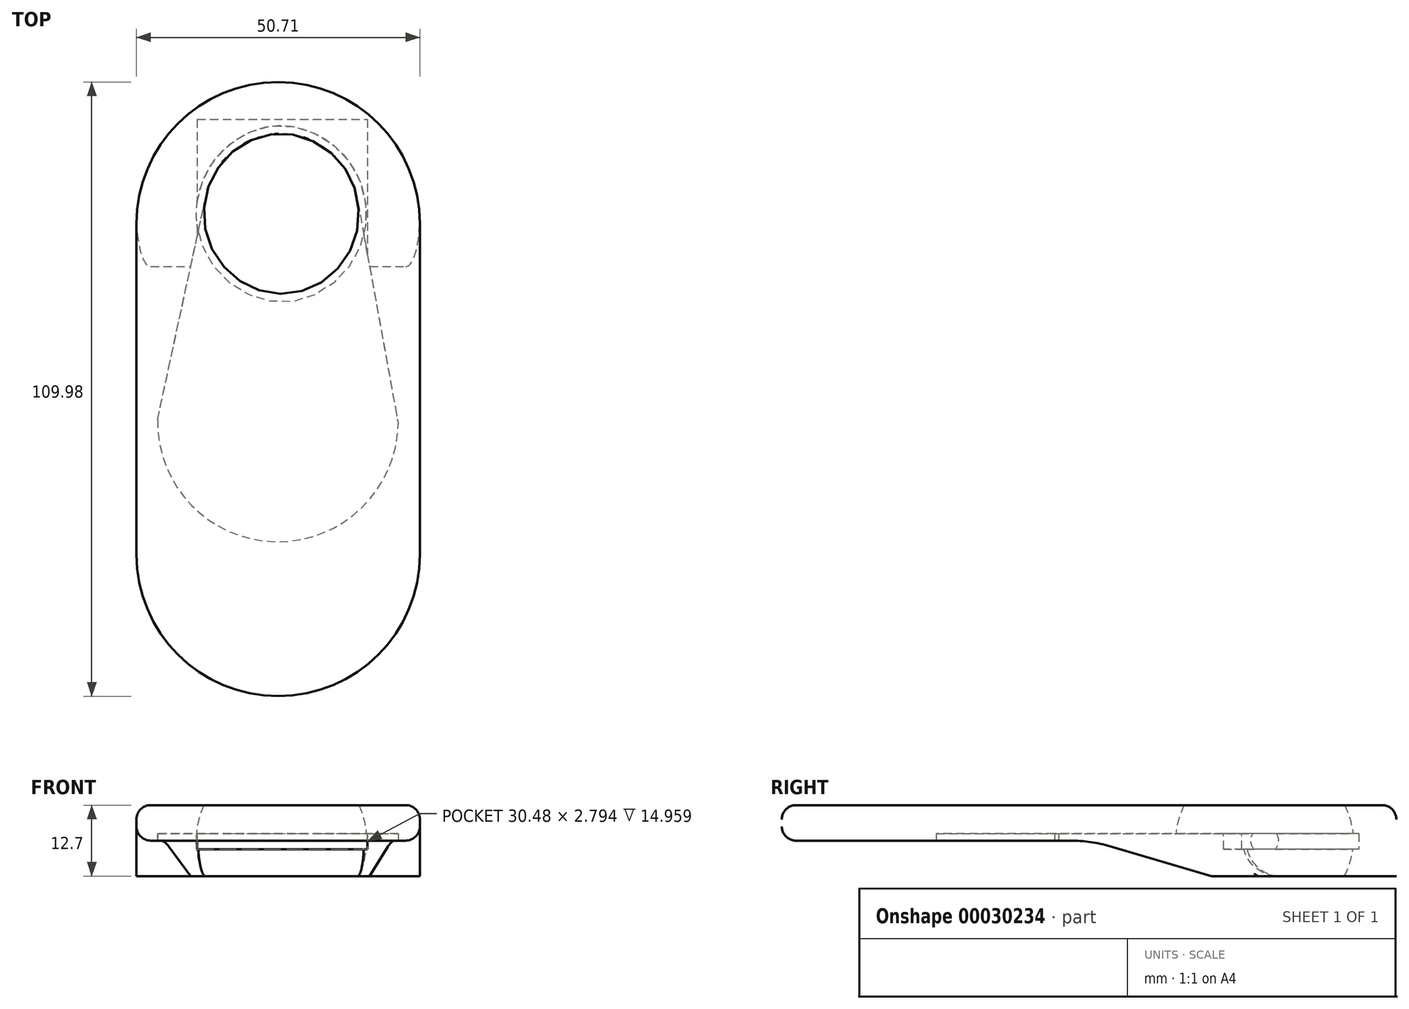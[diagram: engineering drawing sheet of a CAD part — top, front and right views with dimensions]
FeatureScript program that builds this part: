
annotation { "Feature Type Name" : "Feature", "Feature Type Description" : "" }
export const myFeature = defineFeature(function(context is Context, id is Id, definition is map)
    precondition{}
    {
        {
            var Q0;
            Q0=qCreatedBy(makeId("Top.planeOp"),FACE);
            var sketch = newSketch(context, id + "F0", { "sketchPlane" : qUnion([Q0])});
            skLineSegment(sketch, "E0.bottom", {"start": v(-12.22, 60.39) * mm, "end": v(18.26, 60.39) * mm});
            skLineSegment(sketch, "E0.top", {"start": v(-12.22, 28.64) * mm, "end": v(18.26, 28.64) * mm});
            skLineSegment(sketch, "E0.left", {"start": v(-12.22, 60.39) * mm, "end": v(-12.22, 28.64) * mm});
            skLineSegment(sketch, "E0.right", {"start": v(18.26, 60.39) * mm, "end": v(18.26, 28.64) * mm});
            skSolve(sketch);
        }
        {
            var Q0;
            Q0=qCreatedBy(makeId("Top.planeOp"),FACE);
            var sketch = newSketch(context, id + "F1", { "sketchPlane" : qUnion([Q0])});
            skArc(sketch, "E1", {"start": v(3.76, 27.52) * mm, "mid": v(18.06, 44.36) * mm, "end": v(1.92, 59.44) * mm});
            skLineSegment(sketch, "E2", {"start": v(3.76, 27.52) * mm, "end": v(1.92, 59.44) * mm});
            skSolve(sketch);
        }
        {
            var Q0;
            Q0=makeQuery(id+"F1.imprint","IMPRINT",FACE,{"disambiguationData":[TD([[makeQuery(id+"F1.imprint","IMPRINT",EDGE,{"derivedFrom":sQuery(id+"F1.wireOp",EDGE,"E1")}),1.0]])]});
            var Q1;
            Q1=sQuery(id+"F1.wireOp",EDGE,"E1");
            var Q2;
            Q2=sQuery(id+"F1.wireOp",EDGE,"E2");
            revolve(context, id + "F2", {"entities" : qUnion([Q0]), "surfaceEntities" : qUnion([Q1]), "axis" : qUnion([Q2]), "revolveType" : RevolveType.FULL});
        }
        {
            var Q0;
            Q0=makeQuery(id+"F0.imprint","IMPRINT",FACE,{"disambiguationData":[TD([[makeQuery(id+"F0.imprint","IMPRINT",EDGE,{"derivedFrom":sQuery(id+"F0.wireOp",EDGE,"E0.bottom")}),-1.0]])]});
            extrude(context, id + "F3", {"entities" : qUnion([Q0]), "depth" : 1.27 * mm, "hasSecondDirection" : true, "secondDirectionOppositeDirection" : true, "secondDirectionDepth" : 1.52 * mm});
        }
        {
            var Q0;
            Q0=qCreatedBy(makeId("Top.planeOp"),FACE);
            var sketch = newSketch(context, id + "F4", { "sketchPlane" : qUnion([Q0])});
            skLineSegment(sketch, "E3.bottom", {"start": v(-23.08, 67.1) * mm, "end": v(27.63, 67.1) * mm});
            skLineSegment(sketch, "E3.top", {"start": v(-23.08, -42.89) * mm, "end": v(27.63, -42.89) * mm});
            skLineSegment(sketch, "E3.left", {"start": v(-23.08, 67.1) * mm, "end": v(-23.08, -42.89) * mm});
            skLineSegment(sketch, "E3.right", {"start": v(27.63, 67.1) * mm, "end": v(27.63, -42.89) * mm});
            skSolve(sketch);
        }
        {
            var Q0;
            Q0=makeQuery(id+"F4.imprint","IMPRINT",FACE,{"disambiguationData":[TD([[makeQuery(id+"F4.imprint","IMPRINT",EDGE,{"derivedFrom":sQuery(id+"F4.wireOp",EDGE,"E3.bottom")}),-1.0]])]});
            extrude(context, id + "F5", {"entities" : qUnion([Q0]), "depth" : 6.35 * mm, "hasSecondDirection" : true, "secondDirectionOppositeDirection" : true, "secondDirectionDepth" : 6.35 * mm});
        }
        {
            var Q0;
            Q0=makeQuery(id+"F2.opRevolve","SWEPT_BODY",BODY,{"disambiguationData":[OSD([sQuery(id+"F1.wireOp",EDGE,"E1"),sQuery(id+"F1.wireOp",EDGE,"E2")])]});
            var Q1;
            Q1=makeQuery(id+"F3.opExtrude","SWEPT_BODY",BODY,{"disambiguationData":[OSD([sQuery(id+"F0.wireOp",EDGE,"E0.bottom"),sQuery(id+"F0.wireOp",EDGE,"E0.top"),sQuery(id+"F0.wireOp",EDGE,"E0.left"),sQuery(id+"F0.wireOp",EDGE,"E0.right")])]});
            booleanBodies(context, id + "F6", {"operationType" : BooleanOperationType.UNION, "tools" : qUnion([Q0, Q1])});
        }
        {
            var Q0;
            Q0=makeQuery(id+"F2.opRevolve","SWEPT_BODY",BODY,{"disambiguationData":[OSD([sQuery(id+"F1.wireOp",EDGE,"E1"),sQuery(id+"F1.wireOp",EDGE,"E2")])]});
            var Q1;
            Q1=makeQuery(id+"F5.opExtrude","SWEPT_BODY",BODY,{"disambiguationData":[OSD([sQuery(id+"F4.wireOp",EDGE,"E3.bottom"),sQuery(id+"F4.wireOp",EDGE,"E3.top"),sQuery(id+"F4.wireOp",EDGE,"E3.left"),sQuery(id+"F4.wireOp",EDGE,"E3.right")])]});
            booleanBodies(context, id + "F7", {"operationType" : BooleanOperationType.SUBTRACTION, "tools" : qUnion([Q0]), "targets" : qUnion([Q1])});
        }
        {
            var Q0;
            Q0=makeQuery(id+"F5.opExtrude","CAP_FACE",FACE,{"disambiguationData":[OSD([sQuery(id+"F4.wireOp",EDGE,"E3.bottom"),sQuery(id+"F4.wireOp",EDGE,"E3.top"),sQuery(id+"F4.wireOp",EDGE,"E3.left"),sQuery(id+"F4.wireOp",EDGE,"E3.right")])],"isStart":true});
            var sketch = newSketch(context, id + "F8", { "sketchPlane" : qUnion([Q0])});
            skArc(sketch, "E4", {"start": v(23.75, -5.94) * mm, "mid": v(1.86, 15.23) * mm, "end": v(-19.31, -6.66) * mm});
            skLineSegment(sketch, "E5", {"start": v(-19.31, -6.66) * mm, "end": v(-10.88, -45.61) * mm});
            skLineSegment(sketch, "E6", {"start": v(-10.88, -45.61) * mm, "end": v(16.54, -45.61) * mm});
            skLineSegment(sketch, "E7", {"start": v(16.54, -45.61) * mm, "end": v(23.75, -5.94) * mm});
            skSolve(sketch);
        }
        {
            var Q0;
            {var subQ4=sQuery(id+"F8.wireOp",EDGE,"E4");Q0=makeQuery(id+"F8.imprint","IMPRINT",FACE,{"disambiguationData":[TD([[makeQuery(id+"F8.imprint","IMPRINT",EDGE,{"derivedFrom":subQ4}),1.0]])]});}
            extrude(context, id + "F9", {"entities" : qUnion([Q0]), "operationType" : NewBodyOperationType.REMOVE, "oppositeDirection" : true, "depth" : 7.62 * mm});
        }
        {
            var Q0;
            Q0=makeQuery(id+"F5.opExtrude","SWEPT_FACE",FACE,{"disambiguationData":[OSD([sQuery(id+"F4.wireOp",EDGE,"E3.right")])]});
            var sketch = newSketch(context, id + "F10", { "sketchPlane" : qUnion([Q0])});
            skLineSegment(sketch, "E8", {"start": v(34.01, -6.35) * mm, "end": v(12.4, 0) * mm});
            skLineSegment(sketch, "E9", {"start": v(12.4, 0) * mm, "end": v(-42.89, 0) * mm});
            skLineSegment(sketch, "E10", {"start": v(-42.89, 0) * mm, "end": v(-42.89, -6.35) * mm});
            skLineSegment(sketch, "E11", {"start": v(-42.89, -6.35) * mm, "end": v(34.01, -6.35) * mm});
            skSolve(sketch);
        }
        {
            var Q0;
            Q0=makeQuery(id+"F10.imprint","IMPRINT",FACE,{"disambiguationData":[TD([[makeQuery(id+"F10.imprint","IMPRINT",EDGE,{"derivedFrom":sQuery(id+"F10.wireOp",EDGE,"E8")}),1.0]])]});
            extrude(context, id + "F11", {"entities" : qUnion([Q0]), "operationType" : NewBodyOperationType.REMOVE, "endBound" : BoundingType.THROUGH_ALL, "oppositeDirection" : true, "depth" : 25.4 * mm});
        }
        {
            var Q0;
            Q0=makeQuery(id+"F5.opExtrude","SWEPT_EDGE",EDGE,{"disambiguationData":[OSD([sQuery(id+"F4.wireOp",EDGE,"E3.top"),sQuery(id+"F4.wireOp",EDGE,"E3.right")])]});
            var Q1;
            Q1=makeQuery(id+"F5.opExtrude","SWEPT_EDGE",EDGE,{"disambiguationData":[OSD([sQuery(id+"F4.wireOp",EDGE,"E3.top"),sQuery(id+"F4.wireOp",EDGE,"E3.left")])]});
            var Q2;
            Q2=makeQuery(id+"F5.opExtrude","SWEPT_EDGE",EDGE,{"disambiguationData":[OSD([sQuery(id+"F4.wireOp",EDGE,"E3.bottom"),sQuery(id+"F4.wireOp",EDGE,"E3.right")])]});
            var Q3;
            Q3=makeQuery(id+"F5.opExtrude","SWEPT_EDGE",EDGE,{"disambiguationData":[OSD([sQuery(id+"F4.wireOp",EDGE,"E3.bottom"),sQuery(id+"F4.wireOp",EDGE,"E3.left")])]});
            fillet(context, id + "F12", {"entities" : qUnion([Q0, Q1, Q2, Q3]), "radius" : 25.4 * mm, "tangentPropagation" : true, "allowEdgeOverflow" : false});
        }
        {
            var Q0;
            Q0=makeQuery(id+"F11.boolean.opBoolean","COPY",EDGE,{"disambiguationData":[OD(1.0)],"derivedFrom":makeQuery(id+"F11.opExtrude","SWEPT_EDGE",EDGE,{"disambiguationData":[OSD([sQuery(id+"F4.wireOp",EDGE,"E3.right"),sQuery(id+"F10.wireOp",EDGE,"E8"),sQuery(id+"F10.wireOp",EDGE,"E11")])]})});
            var Q1;
            Q1=makeQuery(id+"F11.boolean.opBoolean","COPY",EDGE,{"disambiguationData":[OD(0.0)],"derivedFrom":makeQuery(id+"F11.opExtrude","SWEPT_EDGE",EDGE,{"disambiguationData":[OSD([sQuery(id+"F4.wireOp",EDGE,"E3.right"),sQuery(id+"F10.wireOp",EDGE,"E8"),sQuery(id+"F10.wireOp",EDGE,"E11")])]})});
            var Q2;
            Q2=makeQuery(id+"F11.boolean.opBoolean","COPY",EDGE,{"disambiguationData":[OD(0.0)],"derivedFrom":makeQuery(id+"F11.opExtrude","SWEPT_EDGE",EDGE,{"disambiguationData":[OSD([sQuery(id+"F10.wireOp",EDGE,"E8"),sQuery(id+"F10.wireOp",EDGE,"E9")])]})});
            var Q3;
            Q3=makeQuery(id+"F11.boolean.opBoolean","COPY",EDGE,{"disambiguationData":[OD(1.0)],"derivedFrom":makeQuery(id+"F11.opExtrude","SWEPT_EDGE",EDGE,{"disambiguationData":[OSD([sQuery(id+"F10.wireOp",EDGE,"E8"),sQuery(id+"F10.wireOp",EDGE,"E9")])]})});
            fillet(context, id + "F13", {"entities" : qUnion([Q0, Q1, Q2, Q3]), "radius" : 25.4 * mm, "tangentPropagation" : true, "allowEdgeOverflow" : false});
        }
        {
            var Q0;
            Q0=makeQuery(id+"F11.boolean.opBoolean","COPY",EDGE,{"derivedFrom":makeQuery(id+"F11.opExtrude","CAP_EDGE",EDGE,{"disambiguationData":[OSD([sQuery(id+"F10.wireOp",EDGE,"E9")])],"isStart":true})});
            var Q1;
            Q1=makeQuery(id+"F12.opFillet","BLEND_EDGE",EDGE,{"blendedFrom":[makeQuery(id+"F5.opExtrude","SWEPT_EDGE",EDGE,{"disambiguationData":[OSD([sQuery(id+"F4.wireOp",EDGE,"E3.top"),sQuery(id+"F4.wireOp",EDGE,"E3.right")])]}),makeQuery(id+"F11.boolean.opBoolean","COPY",FACE,{"derivedFrom":makeQuery(id+"F11.opExtrude","SWEPT_FACE",FACE,{"disambiguationData":[OSD([sQuery(id+"F10.wireOp",EDGE,"E9")])]})})],"blendedInto":[makeQuery(id+"F11.boolean.opBoolean","COPY",FACE,{"derivedFrom":makeQuery(id+"F11.opExtrude","SWEPT_FACE",FACE,{"disambiguationData":[OSD([sQuery(id+"F10.wireOp",EDGE,"E9")])]})})]});
            var Q2;
            Q2=makeQuery(id+"F12.opFillet","BLEND_EDGE",EDGE,{"blendedFrom":[makeQuery(id+"F5.opExtrude","SWEPT_EDGE",EDGE,{"disambiguationData":[OSD([sQuery(id+"F4.wireOp",EDGE,"E3.top"),sQuery(id+"F4.wireOp",EDGE,"E3.left")])]}),makeQuery(id+"F11.boolean.opBoolean","COPY",FACE,{"derivedFrom":makeQuery(id+"F11.opExtrude","SWEPT_FACE",FACE,{"disambiguationData":[OSD([sQuery(id+"F10.wireOp",EDGE,"E9")])]})})],"blendedInto":[makeQuery(id+"F11.boolean.opBoolean","COPY",FACE,{"derivedFrom":makeQuery(id+"F11.opExtrude","SWEPT_FACE",FACE,{"disambiguationData":[OSD([sQuery(id+"F10.wireOp",EDGE,"E9")])]})})]});
            var Q3;
            Q3=makeQuery(id+"F5.opExtrude","CAP_EDGE",EDGE,{"disambiguationData":[OSD([sQuery(id+"F4.wireOp",EDGE,"E3.right")])],"isStart":false});
            var Q4;
            Q4=makeQuery(id+"F5.opExtrude","CAP_EDGE",EDGE,{"disambiguationData":[OSD([sQuery(id+"F4.wireOp",EDGE,"E3.left")])],"isStart":false});
            var Q5;
            {var subQ0=sQuery(id+"F4.wireOp",EDGE,"E3.top");var subQ1=sQuery(id+"F4.wireOp",EDGE,"E3.left");Q5=makeQuery(id+"F12.opFillet","BLEND_EDGE",EDGE,{"blendedFrom":[makeQuery(id+"F5.opExtrude","SWEPT_EDGE",EDGE,{"disambiguationData":[OSD([subQ0,subQ1])]}),makeQuery(id+"F5.opExtrude","CAP_FACE",FACE,{"disambiguationData":[OSD([sQuery(id+"F4.wireOp",EDGE,"E3.bottom"),subQ0,subQ1,sQuery(id+"F4.wireOp",EDGE,"E3.right")])],"isStart":false})],"blendedInto":[makeQuery(id+"F5.opExtrude","CAP_FACE",FACE,{"disambiguationData":[OSD([sQuery(id+"F4.wireOp",EDGE,"E3.bottom"),subQ0,subQ1,sQuery(id+"F4.wireOp",EDGE,"E3.right")])],"isStart":false})]});}
            var Q6;
            {var subQ0=sQuery(id+"F4.wireOp",EDGE,"E3.top");var subQ1=sQuery(id+"F4.wireOp",EDGE,"E3.right");Q6=makeQuery(id+"F12.opFillet","BLEND_EDGE",EDGE,{"blendedFrom":[makeQuery(id+"F5.opExtrude","SWEPT_EDGE",EDGE,{"disambiguationData":[OSD([subQ0,subQ1])]}),makeQuery(id+"F5.opExtrude","CAP_FACE",FACE,{"disambiguationData":[OSD([sQuery(id+"F4.wireOp",EDGE,"E3.bottom"),subQ0,sQuery(id+"F4.wireOp",EDGE,"E3.left"),subQ1])],"isStart":false})],"blendedInto":[makeQuery(id+"F5.opExtrude","CAP_FACE",FACE,{"disambiguationData":[OSD([sQuery(id+"F4.wireOp",EDGE,"E3.bottom"),subQ0,sQuery(id+"F4.wireOp",EDGE,"E3.left"),subQ1])],"isStart":false})]});}
            var Q7;
            {var subQ0=sQuery(id+"F4.wireOp",EDGE,"E3.bottom");var subQ1=sQuery(id+"F4.wireOp",EDGE,"E3.right");Q7=makeQuery(id+"F12.opFillet","BLEND_EDGE",EDGE,{"blendedFrom":[makeQuery(id+"F5.opExtrude","SWEPT_EDGE",EDGE,{"disambiguationData":[OSD([subQ0,subQ1])]}),makeQuery(id+"F5.opExtrude","CAP_FACE",FACE,{"disambiguationData":[OSD([subQ0,sQuery(id+"F4.wireOp",EDGE,"E3.top"),sQuery(id+"F4.wireOp",EDGE,"E3.left"),subQ1])],"isStart":false})],"blendedInto":[makeQuery(id+"F5.opExtrude","CAP_FACE",FACE,{"disambiguationData":[OSD([subQ0,sQuery(id+"F4.wireOp",EDGE,"E3.top"),sQuery(id+"F4.wireOp",EDGE,"E3.left"),subQ1])],"isStart":false})]});}
            var Q8;
            {var subQ0=sQuery(id+"F4.wireOp",EDGE,"E3.bottom");var subQ1=sQuery(id+"F4.wireOp",EDGE,"E3.left");Q8=makeQuery(id+"F12.opFillet","BLEND_EDGE",EDGE,{"blendedFrom":[makeQuery(id+"F5.opExtrude","SWEPT_EDGE",EDGE,{"disambiguationData":[OSD([subQ0,subQ1])]}),makeQuery(id+"F5.opExtrude","CAP_FACE",FACE,{"disambiguationData":[OSD([subQ0,sQuery(id+"F4.wireOp",EDGE,"E3.top"),subQ1,sQuery(id+"F4.wireOp",EDGE,"E3.right")])],"isStart":false})],"blendedInto":[makeQuery(id+"F5.opExtrude","CAP_FACE",FACE,{"disambiguationData":[OSD([subQ0,sQuery(id+"F4.wireOp",EDGE,"E3.top"),subQ1,sQuery(id+"F4.wireOp",EDGE,"E3.right")])],"isStart":false})]});}
            fillet(context, id + "F14", {"entities" : qUnion([Q0, Q1, Q2, Q3, Q4, Q5, Q6, Q7, Q8]), "radius" : 2.54 * mm, "tangentPropagation" : true, "allowEdgeOverflow" : false});
        }
        {
            var Q0;
            Q0=makeQuery(id+"F5.opExtrude","CAP_FACE",FACE,{"disambiguationData":[OSD([sQuery(id+"F4.wireOp",EDGE,"E3.bottom"),sQuery(id+"F4.wireOp",EDGE,"E3.top"),sQuery(id+"F4.wireOp",EDGE,"E3.left"),sQuery(id+"F4.wireOp",EDGE,"E3.right")])],"isStart":false});
            var sketch = newSketch(context, id + "F15", { "sketchPlane" : qUnion([Q0])});
            skFitSpline(sketch, "E12", {"points": [v(-8.59, -5.22) * mm, v(-6.1, 0) * mm, v(1.73, 2.73) * mm, v(8.75, 1.7) * mm, v(14.01, -2.85) * mm, v(14.32, -8.31) * mm, v(11.02, -12.03) * mm, v(4.62, -14.3) * mm, v(-1.05, -14.1) * mm, v(-6, -11.41) * mm, v(-8.59, -5.22) * mm]});
            skFitSpline(sketch, "E13", {"points": [v(7.2, -16.05) * mm, v(5.14, -18.94) * mm, v(5.45, -19.98) * mm, v(7, -19.67) * mm, v(10.1, -14.71) * mm, v(9.68, -13.89) * mm, v(8.9, -13.1) * mm], "startDerivative": vector(-12.9, -14.2) * mm, "endDerivative": vector(-6.51, 6.69) * mm});
            skFitSpline(sketch, "E14", {"points": [v(-1.36, -15.44) * mm, v(1.42, -18.84) * mm, v(0.9, -19.56) * mm, v(0, -19.77) * mm, v(-3.94, -14.61) * mm, v(-3.84, -14.1) * mm, v(-3.3, -13.33) * mm], "startDerivative": vector(16.36, -15.84) * mm, "endDerivative": vector(5.04, 7.32) * mm});
            skSolve(sketch);
        }
        {
            var Q0;
            {var subQ0=sQuery(id+"F15.wireOp",EDGE,"E12");var subQ2=makeQuery(id+"F15.imprint","IMPRINT",VERTEX,{"disambiguationData":[OD(0.0)],"derivedFrom":subQ0});Q0=makeQuery(id+"F15.imprint","IMPRINT",FACE,{"disambiguationData":[TD([[makeQuery(id+"F15.imprint","IMPRINT",EDGE,{"disambiguationData":[TD([[subQ2,-1.0]])],"derivedFrom":subQ0}),-1.0]])]});}
            var Q1;
            Q1=sQuery(id+"F15.wireOp",EDGE,"E12");
            var Q2;
            Q2=sQuery(id+"F15.wireOp",EDGE,"E14");
            var Q3;
            Q3=sQuery(id+"F15.wireOp",EDGE,"E13");
            extrude(context, id + "F16", {"entities" : qUnion([Q0]), "operationType" : NewBodyOperationType.REMOVE, "surfaceEntities" : qUnion([Q1, Q2, Q3]), "depth" : 3.17 * mm});
        }
    });
